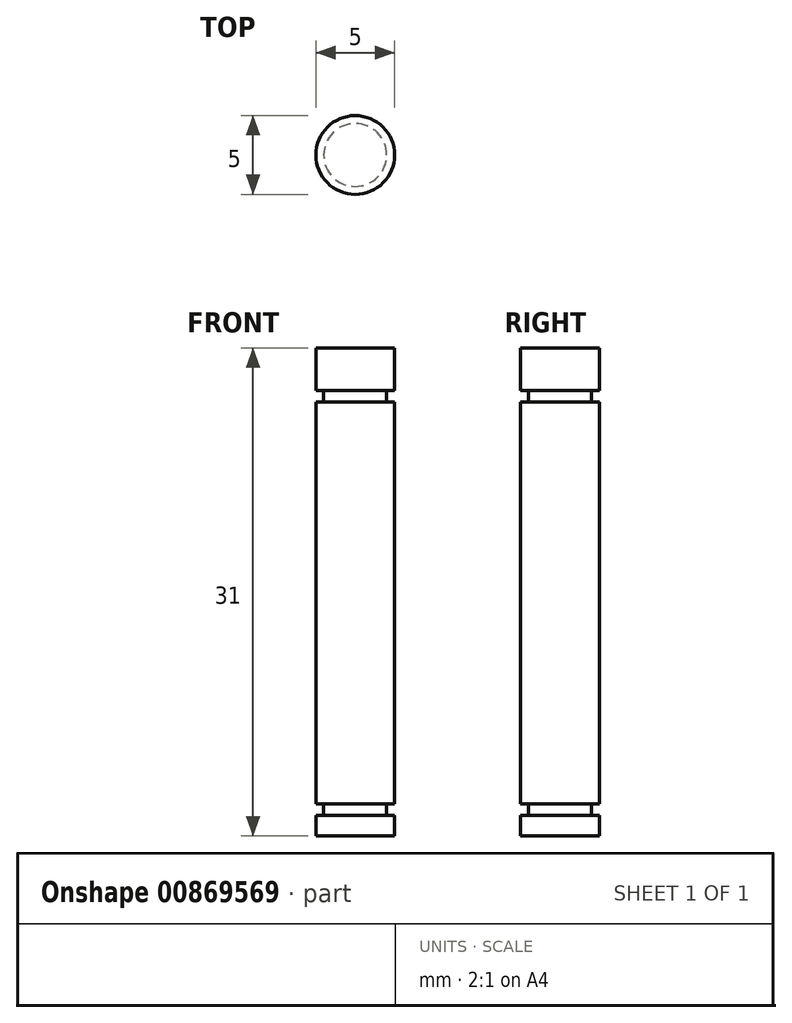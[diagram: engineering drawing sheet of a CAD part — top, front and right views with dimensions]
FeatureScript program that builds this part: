
annotation { "Feature Type Name" : "Feature", "Feature Type Description" : "" }
export const myFeature = defineFeature(function(context is Context, id is Id, definition is map)
    precondition{}
    {
        {
            var Q0;
            Q0=qCreatedBy(makeId("Top.planeOp"),FACE);
            var sketch = newSketch(context, id + "F0", { "sketchPlane" : qUnion([Q0])});
            skCircle(sketch, "E0", {"center": v(0, 0) * mm, "radius": 2.5 * mm});
            skSolve(sketch);
        }
        {
            var Q0;
            Q0 = qSketchRegion(id + "F0", true);
            extrude(context, id + "F1", {"entities" : qUnion([Q0]), "flatOperationType" : FlatOperationType.REMOVE, "depth" : 31 * mm, "offsetDistance" : 25 * mm, "domain" : OperationDomain.MODEL});
        }
        {
            var Q0;
            Q0=makeQuery(id+"F1.opExtrude","CAP_FACE",FACE,{"disambiguationData":[OSD([sQuery(id+"F0.wireOp",EDGE,"E0")])],"isStart":true});
            cPlane(context, id + "F2", {"entities" : qUnion([Q0]), "cplaneType" : CPlaneType.OFFSET, "offset" : 2.28 * mm - 0.13 * mm - 0.38 * mm + .134 * mm - .6 * mm, "oppositeDirection" : true, "width" : 150 * mm, "height" : 150 * mm});
        }
        {
            var Q0;
            Q0=qCreatedBy(id+"F2.planeOp",FACE);
            var sketch = newSketch(context, id + "F3", { "sketchPlane" : qUnion([Q0])});
            skCircle(sketch, "E1", {"center": v(0, 0) * mm, "radius": 2 * mm});
            skCircle(sketch, "E2", {"center": v(0, 0) * mm, "radius": 2.5 * mm});
            skSolve(sketch);
        }
        {
            var Q0;
            Q0 = qSketchRegion(id + "F3", true);
            extrude(context, id + "F4", {"entities" : qUnion([Q0]), "operationType" : NewBodyOperationType.REMOVE, "flatOperationType" : FlatOperationType.REMOVE, "oppositeDirection" : true, "depth" : 0.74 * mm, "offsetDistance" : 25 * mm, "domain" : OperationDomain.MODEL});
        }
        {
            var Q0;
            Q0=qCreatedBy(id+"F2.planeOp",FACE);
            cPlane(context, id + "F5", {"entities" : qUnion([Q0]), "cplaneType" : CPlaneType.OFFSET, "offset" : 25.74 * mm + 0.5 * mm, "oppositeDirection" : true, "width" : 150 * mm, "height" : 150 * mm});
        }
        {
            var Q0;
            Q0=qCreatedBy(id+"F5.planeOp",FACE);
            var sketch = newSketch(context, id + "F6", { "sketchPlane" : qUnion([Q0])});
            skCircle(sketch, "E3", {"center": v(0, 0) * mm, "radius": 2 * mm});
            skCircle(sketch, "E4", {"center": v(0, 0) * mm, "radius": 2.5 * mm});
            skSolve(sketch);
        }
        {
            var Q0;
            Q0 = qSketchRegion(id + "F6", true);
            extrude(context, id + "F7", {"entities" : qUnion([Q0]), "operationType" : NewBodyOperationType.REMOVE, "flatOperationType" : FlatOperationType.REMOVE, "oppositeDirection" : true, "depth" : .74 * mm, "offsetDistance" : 25 * mm, "domain" : OperationDomain.MODEL});
        }
    });
